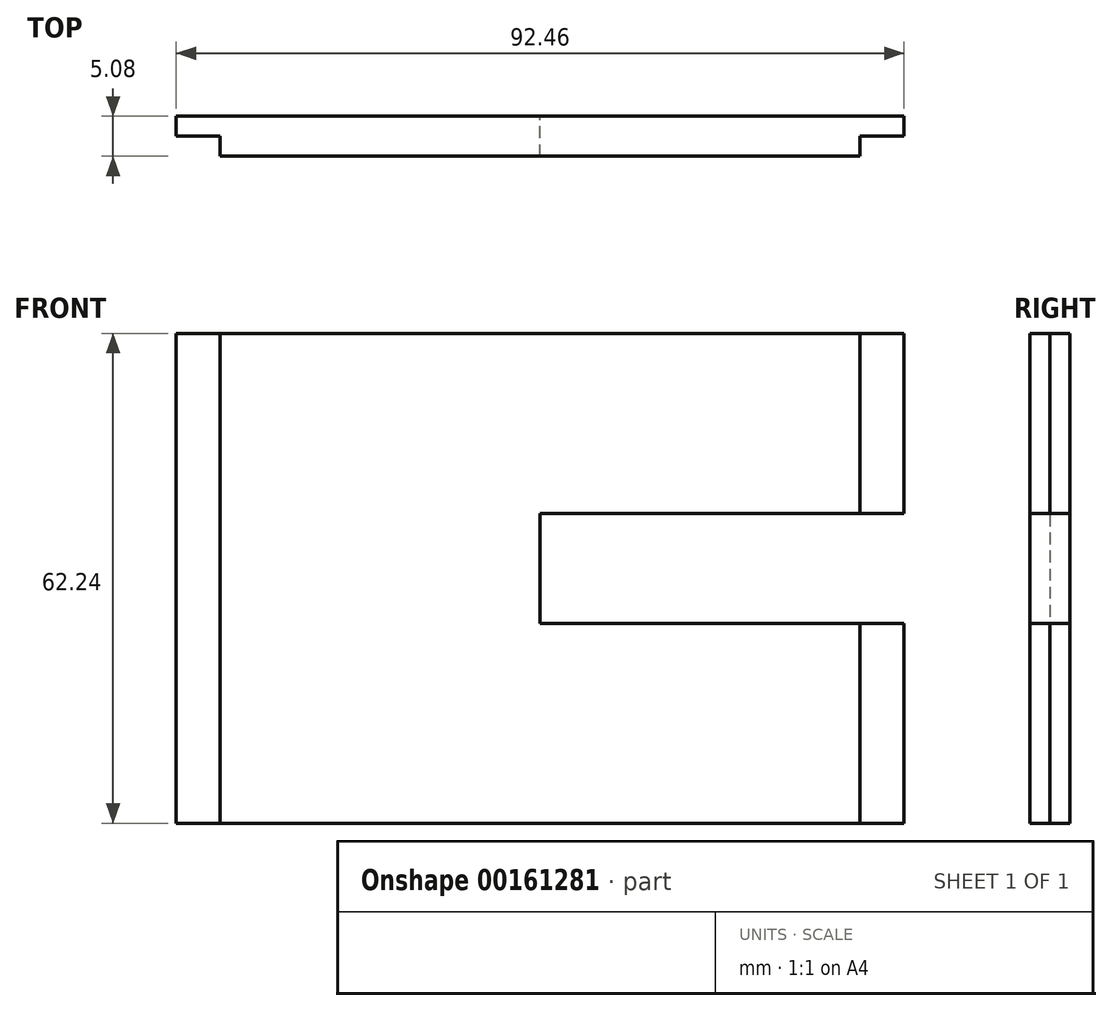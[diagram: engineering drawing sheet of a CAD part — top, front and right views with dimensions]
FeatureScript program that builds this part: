
annotation { "Feature Type Name" : "Feature", "Feature Type Description" : "" }
export const myFeature = defineFeature(function(context is Context, id is Id, definition is map)
    precondition{}
    {
        {
            var Q0;
            Q0=qCreatedBy(makeId("Front.planeOp"),FACE);
            var sketch = newSketch(context, id + "F0", { "sketchPlane" : qUnion([Q0])});
            skLineSegment(sketch, "E0.bottom", {"start": v(40.64, 31.11) * mm, "end": v(-40.64, 31.12) * mm});
            skLineSegment(sketch, "E0.top", {"start": v(40.64, -31.12) * mm, "end": v(-40.64, -31.11) * mm});
            skPoint(sketch, "E0.middle", {"position": v(0, 0) * mm});
            skLineSegment(sketch, "E1", {"start": v(40.64, 8.26) * mm, "end": v(0, 8.25) * mm});
            skLineSegment(sketch, "E2", {"start": v(0, 8.25) * mm, "end": v(0, -5.72) * mm});
            skLineSegment(sketch, "E3", {"start": v(0, -5.72) * mm, "end": v(40.64, -5.71) * mm});
            skLineSegment(sketch, "E4", {"start": v(-40.64, 31.12) * mm, "end": v(-40.64, -31.11) * mm});
            skLineSegment(sketch, "E5", {"start": v(40.64, 31.12) * mm, "end": v(40.64, 8.26) * mm});
            skLineSegment(sketch, "E6", {"start": v(40.64, -5.71) * mm, "end": v(40.64, -31.12) * mm});
            skSolve(sketch);
        }
        {
            var Q0;
            Q0=makeQuery(id+"F0.imprint","IMPRINT",FACE,{"disambiguationData":[TD([[makeQuery(id+"F0.imprint","IMPRINT",EDGE,{"derivedFrom":sQuery(id+"F0.wireOp",EDGE,"E0.bottom")}),1.0]])]});
            extrude(context, id + "F1", {"entities" : qUnion([Q0]), "depth" : 2.54 * mm});
        }
        {
            var Q0;
            Q0=makeQuery(id+"F1.opExtrude","CAP_FACE",FACE,{"disambiguationData":[OSD([sQuery(id+"F0.wireOp",EDGE,"E0.bottom"),sQuery(id+"F0.wireOp",EDGE,"E0.top"),sQuery(id+"F0.wireOp",EDGE,"E1"),sQuery(id+"F0.wireOp",EDGE,"E2"),sQuery(id+"F0.wireOp",EDGE,"E3"),sQuery(id+"F0.wireOp",EDGE,"E4"),sQuery(id+"F0.wireOp",EDGE,"E5"),sQuery(id+"F0.wireOp",EDGE,"E6")])],"isStart":true});
            var sketch = newSketch(context, id + "F2", { "sketchPlane" : qUnion([Q0])});
            skLineSegment(sketch, "E7.bottom", {"start": v(-40.64, 31.12) * mm, "end": v(-46.23, 31.12) * mm});
            skLineSegment(sketch, "E7.top", {"start": v(-40.64, 8.26) * mm, "end": v(-46.23, 8.26) * mm});
            skLineSegment(sketch, "E7.left", {"start": v(-40.64, 31.12) * mm, "end": v(-40.64, 8.26) * mm});
            skLineSegment(sketch, "E7.right", {"start": v(-46.23, 31.12) * mm, "end": v(-46.23, 8.26) * mm});
            skLineSegment(sketch, "E8.bottom", {"start": v(-40.64, -5.71) * mm, "end": v(-46.23, -5.71) * mm});
            skLineSegment(sketch, "E8.top", {"start": v(-40.64, -31.12) * mm, "end": v(-46.23, -31.12) * mm});
            skLineSegment(sketch, "E8.left", {"start": v(-40.64, -5.71) * mm, "end": v(-40.64, -31.12) * mm});
            skLineSegment(sketch, "E8.right", {"start": v(-46.23, -5.71) * mm, "end": v(-46.23, -31.12) * mm});
            skLineSegment(sketch, "E9.bottom", {"start": v(40.64, 31.12) * mm, "end": v(46.23, 31.12) * mm});
            skLineSegment(sketch, "E9.top", {"start": v(40.64, -31.11) * mm, "end": v(46.23, -31.11) * mm});
            skLineSegment(sketch, "E9.left", {"start": v(40.64, 31.12) * mm, "end": v(40.64, -31.11) * mm});
            skLineSegment(sketch, "E9.right", {"start": v(46.23, 31.12) * mm, "end": v(46.23, -31.11) * mm});
            skSolve(sketch);
        }
        {
            var Q0;
            {var subQ3=sQuery(id+"F2.wireOp",EDGE,"E7.bottom");Q0=makeQuery(id+"F2.imprint","IMPRINT",FACE,{"disambiguationData":[TD([[makeQuery(id+"F2.imprint","IMPRINT",EDGE,{"derivedFrom":subQ3}),1.0]])]});}
            var Q1;
            {var subQ4=sQuery(id+"F2.wireOp",EDGE,"E8.left");Q1=makeQuery(id+"F2.imprint","IMPRINT",FACE,{"disambiguationData":[TD([[makeQuery(id+"F2.imprint","IMPRINT",EDGE,{"derivedFrom":subQ4}),1.0]])]});}
            var Q2;
            Q2=makeQuery(id+"F2.imprint","IMPRINT",FACE,{"disambiguationData":[TD([[makeQuery(id+"F2.imprint","IMPRINT",EDGE,{"derivedFrom":sQuery(id+"F2.wireOp",EDGE,"E8.bottom")}),1.0]])]});
            var Q3;
            Q3=makeQuery(id+"F2.imprint","IMPRINT",FACE,{"disambiguationData":[TD([[makeQuery(id+"F2.imprint","IMPRINT",EDGE,{"derivedFrom":sQuery(id+"F2.wireOp",EDGE,"E9.bottom")}),-1.0]])]});
            extrude(context, id + "F3", {"entities" : qUnion([Q0, Q1, Q2, Q3]), "operationType" : NewBodyOperationType.ADD, "depth" : 2.54 * mm});
        }
    });
